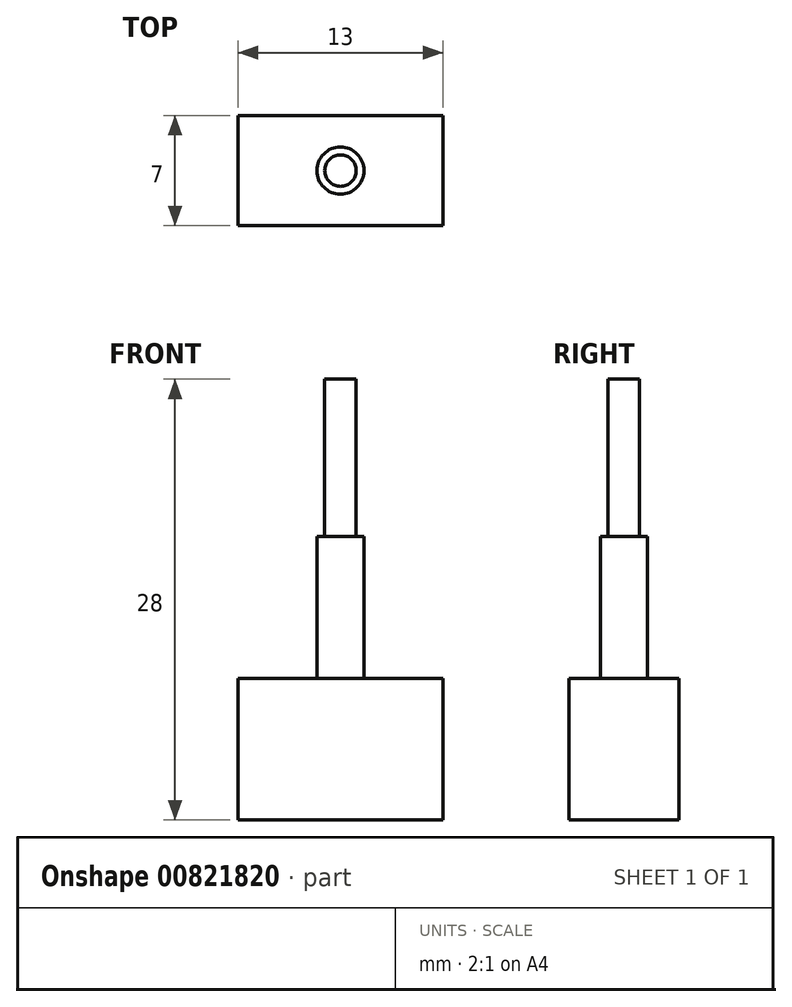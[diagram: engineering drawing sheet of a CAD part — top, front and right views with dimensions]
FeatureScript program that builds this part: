
annotation { "Feature Type Name" : "Feature", "Feature Type Description" : "" }
export const myFeature = defineFeature(function(context is Context, id is Id, definition is map)
    precondition{}
    {
        {
            var Q0;
            Q0=qCreatedBy(makeId("Top.planeOp"),FACE);
            var sketch = newSketch(context, id + "F0", { "sketchPlane" : qUnion([Q0])});
            skLineSegment(sketch, "E0.bottom", {"start": v(6.5, -3.5) * mm, "end": v(-6.5, -3.5) * mm});
            skLineSegment(sketch, "E0.top", {"start": v(6.5, 3.5) * mm, "end": v(-6.5, 3.5) * mm});
            skLineSegment(sketch, "E0.left", {"start": v(6.5, -3.5) * mm, "end": v(6.5, 3.5) * mm});
            skLineSegment(sketch, "E0.right", {"start": v(-6.5, -3.5) * mm, "end": v(-6.5, 3.5) * mm});
            skPoint(sketch, "E0.middle", {"position": v(0, 0) * mm});
            skSolve(sketch);
        }
        {
            var Q0;
            Q0=makeQuery(id+"F0.imprint","IMPRINT",FACE,{"disambiguationData":[TD([[makeQuery(id+"F0.imprint","IMPRINT",EDGE,{"derivedFrom":sQuery(id+"F0.wireOp",EDGE,"E0.bottom")}),-1.0]])]});
            extrude(context, id + "F1", {"entities" : qUnion([Q0]), "depth" : 9 * mm, "offsetDistance" : 25 * mm});
        }
        {
            var Q0;
            Q0=makeQuery(id+"F1.opExtrude","CAP_FACE",FACE,{"disambiguationData":[OSD([sQuery(id+"F0.wireOp",EDGE,"E0.bottom"),sQuery(id+"F0.wireOp",EDGE,"E0.top"),sQuery(id+"F0.wireOp",EDGE,"E0.left"),sQuery(id+"F0.wireOp",EDGE,"E0.right")])],"isStart":false});
            var sketch = newSketch(context, id + "F2", { "sketchPlane" : qUnion([Q0])});
            skCircle(sketch, "E1", {"center": v(0, 0) * mm, "radius": 1.5 * mm});
            skSolve(sketch);
        }
        {
            var Q0;
            Q0=makeQuery(id+"F2.imprint","IMPRINT",FACE,{"disambiguationData":[TD([[makeQuery(id+"F2.imprint","IMPRINT",EDGE,{"derivedFrom":sQuery(id+"F2.wireOp",EDGE,"E1")}),1.0]])]});
            extrude(context, id + "F3", {"entities" : qUnion([Q0]), "operationType" : NewBodyOperationType.ADD, "depth" : 9 * mm, "offsetDistance" : 25 * mm});
        }
        {
            var Q0;
            Q0=makeQuery(id+"F3.opExtrude","CAP_FACE",FACE,{"disambiguationData":[OSD([sQuery(id+"F2.wireOp",EDGE,"E1")])],"isStart":false});
            var sketch = newSketch(context, id + "F4", { "sketchPlane" : qUnion([Q0])});
            skCircle(sketch, "E2", {"center": v(0, 0) * mm, "radius": 1 * mm});
            skSolve(sketch);
        }
        {
            var Q0;
            Q0=makeQuery(id+"F4.imprint","IMPRINT",FACE,{"disambiguationData":[TD([[makeQuery(id+"F4.imprint","IMPRINT",EDGE,{"derivedFrom":sQuery(id+"F4.wireOp",EDGE,"E2")}),1.0]])]});
            extrude(context, id + "F5", {"entities" : qUnion([Q0]), "operationType" : NewBodyOperationType.ADD, "depth" : 10 * mm, "offsetDistance" : 25 * mm});
        }
    });
